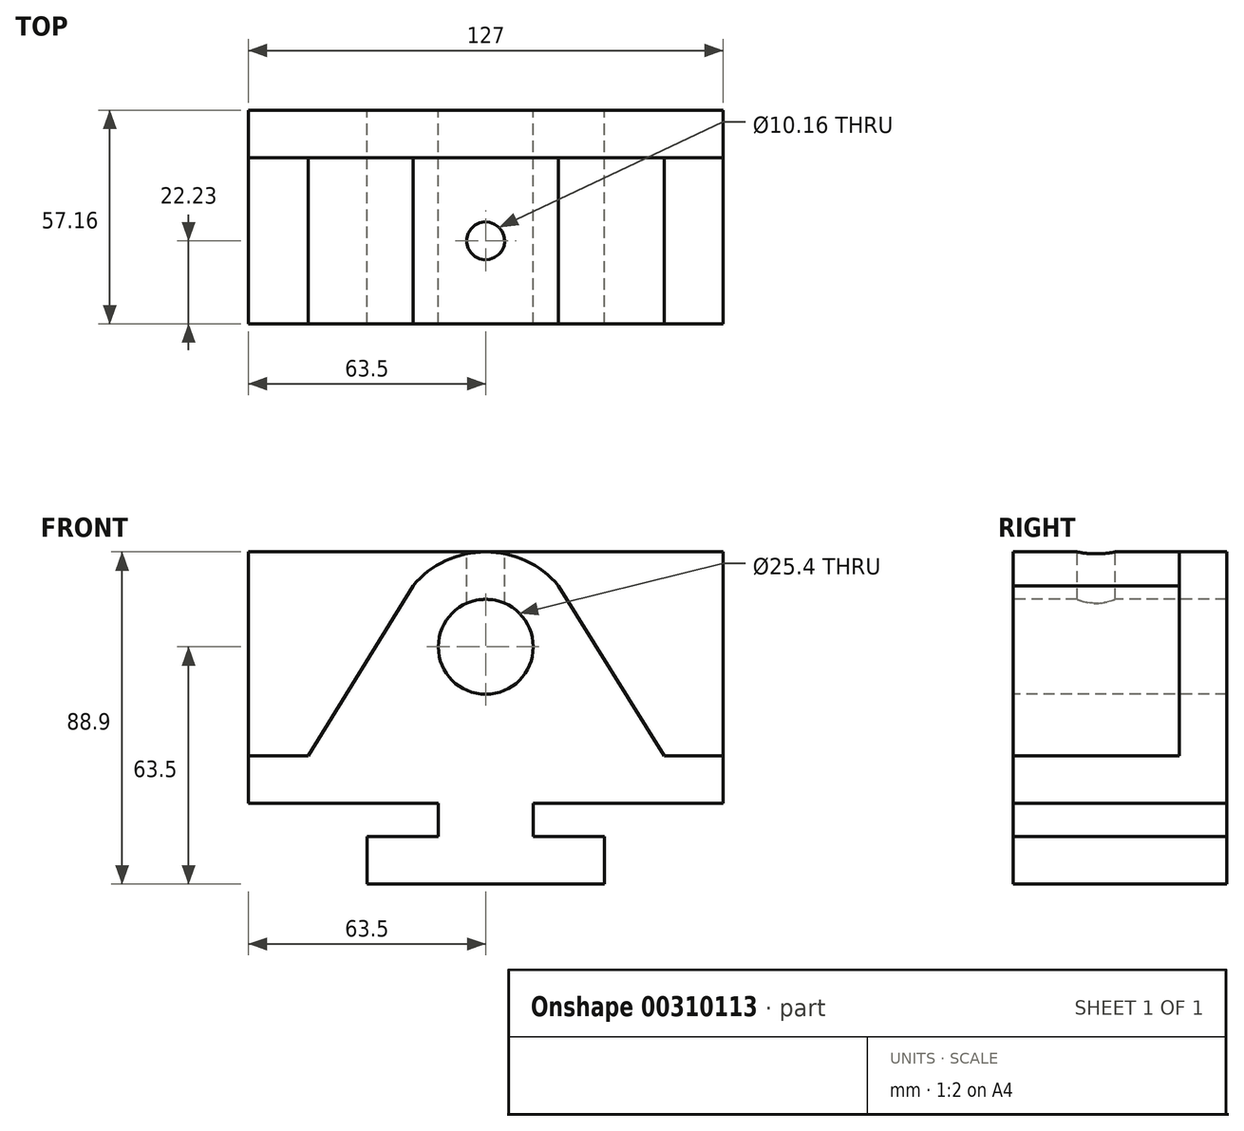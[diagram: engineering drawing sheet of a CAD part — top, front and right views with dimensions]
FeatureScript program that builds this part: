
annotation { "Feature Type Name" : "Feature", "Feature Type Description" : "" }
export const myFeature = defineFeature(function(context is Context, id is Id, definition is map)
    precondition{}
    {
        {
            var Q0;
            Q0=qCreatedBy(makeId("Front.planeOp"),FACE);
            var sketch = newSketch(context, id + "F0", { "sketchPlane" : qUnion([Q0])});
            skLineSegment(sketch, "E0.bottom", {"start": v(31.75, 0) * mm, "end": v(95.25, 0) * mm});
            skLineSegment(sketch, "E0.top", {"start": v(0, 88.9) * mm, "end": v(127, 88.9) * mm});
            skLineSegment(sketch, "E0.left", {"start": v(0, 21.59) * mm, "end": v(0, 88.9) * mm});
            skLineSegment(sketch, "E0.right", {"start": v(127, 21.59) * mm, "end": v(127, 88.9) * mm});
            skLineSegment(sketch, "E1", {"start": v(63.5, 0) * mm, "end": v(63.5, 88.9) * mm, "construction": true});
            skLineSegment(sketch, "E2", {"start": v(95.25, 0) * mm, "end": v(95.25, 12.7) * mm});
            skLineSegment(sketch, "E3", {"start": v(95.25, 12.7) * mm, "end": v(76.2, 12.7) * mm});
            skLineSegment(sketch, "E4", {"start": v(76.2, 12.7) * mm, "end": v(76.2, 21.59) * mm});
            skLineSegment(sketch, "E5", {"start": v(76.2, 21.59) * mm, "end": v(127, 21.59) * mm});
            skLineSegment(sketch, "E6.MirrorCS", {"start": v(31.75, 0) * mm, "end": v(31.75, 12.7) * mm});
            skLineSegment(sketch, "E7.MirrorCS", {"start": v(31.75, 12.7) * mm, "end": v(50.8, 12.7) * mm});
            skLineSegment(sketch, "E8.MirrorCS", {"start": v(50.8, 21.59) * mm, "end": v(0, 21.59) * mm});
            skLineSegment(sketch, "E9.MirrorCS", {"start": v(50.8, 12.7) * mm, "end": v(50.8, 21.59) * mm});
            skPoint(sketch, "E10.orphan", {"position": v(0, 0) * mm});
            skPoint(sketch, "E11.orphan", {"position": v(127, 0) * mm});
            skSolve(sketch);
        }
        {
            var Q0;
            Q0 = qSketchRegion(id + "F0", true);
            extrude(context, id + "F1", {"entities" : qUnion([Q0]), "endBound" : BoundingType.SYMMETRIC, "depth" : 57.15 * mm});
        }
        {
            var Q0;
            Q0=makeQuery(id+"F1.opExtrude","CAP_FACE",FACE,{"disambiguationData":[OSD([sQuery(id+"F0.wireOp",EDGE,"E0.bottom"),sQuery(id+"F0.wireOp",EDGE,"E0.top"),sQuery(id+"F0.wireOp",EDGE,"E0.left"),sQuery(id+"F0.wireOp",EDGE,"E0.right")])],"isStart":false});
            var sketch = newSketch(context, id + "F2", { "sketchPlane" : qUnion([Q0])});
            skLineSegment(sketch, "E12.bottom", {"start": v(0, 34.3) * mm, "end": v(16.04, 34.3) * mm});
            skLineSegment(sketch, "E12.top", {"start": v(0, 88.9) * mm, "end": v(127, 88.9) * mm});
            skLineSegment(sketch, "E12.left", {"start": v(0, 34.3) * mm, "end": v(0, 88.9) * mm});
            skLineSegment(sketch, "E12.right", {"start": v(127, 34.3) * mm, "end": v(127, 88.9) * mm});
            skLineSegment(sketch, "E13", {"start": v(63.5, 0) * mm, "end": v(63.5, 88.9) * mm, "construction": true});
            skLineSegment(sketch, "E14", {"start": v(127, 34.3) * mm, "end": v(111.3, 34.3) * mm});
            skLineSegment(sketch, "E15.trimOffspring", {"start": v(111.3, 34.3) * mm, "end": v(127, 34.3) * mm});
            skArc(sketch, "E16", {"start": v(82.95, 79.84) * mm, "mid": v(63.5, 88.9) * mm, "end": v(44.05, 79.84) * mm});
            skLineSegment(sketch, "E17", {"start": v(16.04, 34.3) * mm, "end": v(44.05, 79.84) * mm});
            skLineSegment(sketch, "E18", {"start": v(82.95, 79.84) * mm, "end": v(111.3, 34.29) * mm});
            skSolve(sketch);
        }
        {
            var Q0;
            Q0 = qSketchRegion(id + "F2", true);
            extrude(context, id + "F3", {"entities" : qUnion([Q0]), "operationType" : NewBodyOperationType.REMOVE, "oppositeDirection" : true, "depth" : 44.45 * mm});
        }
        {
            var Q0;
            Q0=makeQuery(id+"F1.opExtrude","CAP_FACE",FACE,{"disambiguationData":[OSD([sQuery(id+"F0.wireOp",EDGE,"E0.bottom"),sQuery(id+"F0.wireOp",EDGE,"E0.top"),sQuery(id+"F0.wireOp",EDGE,"E0.left"),sQuery(id+"F0.wireOp",EDGE,"E0.right"),sQuery(id+"F0.wireOp",EDGE,"E2"),sQuery(id+"F0.wireOp",EDGE,"E3"),sQuery(id+"F0.wireOp",EDGE,"E4"),sQuery(id+"F0.wireOp",EDGE,"E5"),sQuery(id+"F0.wireOp",EDGE,"E6.MirrorCS"),sQuery(id+"F0.wireOp",EDGE,"E7.MirrorCS"),sQuery(id+"F0.wireOp",EDGE,"E8.MirrorCS"),sQuery(id+"F0.wireOp",EDGE,"E9.MirrorCS")])],"isStart":false});
            var sketch = newSketch(context, id + "F4", { "sketchPlane" : qUnion([Q0])});
            skCircle(sketch, "E19", {"center": v(63.5, 63.5) * mm, "radius": 12.7 * mm});
            skSolve(sketch);
        }
        {
            var Q0;
            Q0 = qSketchRegion(id + "F4", true);
            extrude(context, id + "F5", {"entities" : qUnion([Q0]), "operationType" : NewBodyOperationType.REMOVE, "oppositeDirection" : true, "depth" : 57.15 * mm});
        }
        {
            var Q0;
            Q0=makeQuery(id+"F1.opExtrude","SWEPT_FACE",FACE,{"disambiguationData":[OSD([sQuery(id+"F0.wireOp",EDGE,"E0.top")])]});
            var sketch = newSketch(context, id + "F6", { "sketchPlane" : qUnion([Q0])});
            skLineSegment(sketch, "E20", {"start": v(63.5, 28.58) * mm, "end": v(63.5, -28.96) * mm, "construction": true});
            skCircle(sketch, "E21", {"center": v(63.5, -6.35) * mm, "radius": 5.08 * mm});
            skSolve(sketch);
        }
        {
            var Q0;
            Q0 = qSketchRegion(id + "F6", true);
            extrude(context, id + "F7", {"entities" : qUnion([Q0]), "operationType" : NewBodyOperationType.REMOVE, "oppositeDirection" : true, "depth" : 25.4 * mm});
        }
    });
